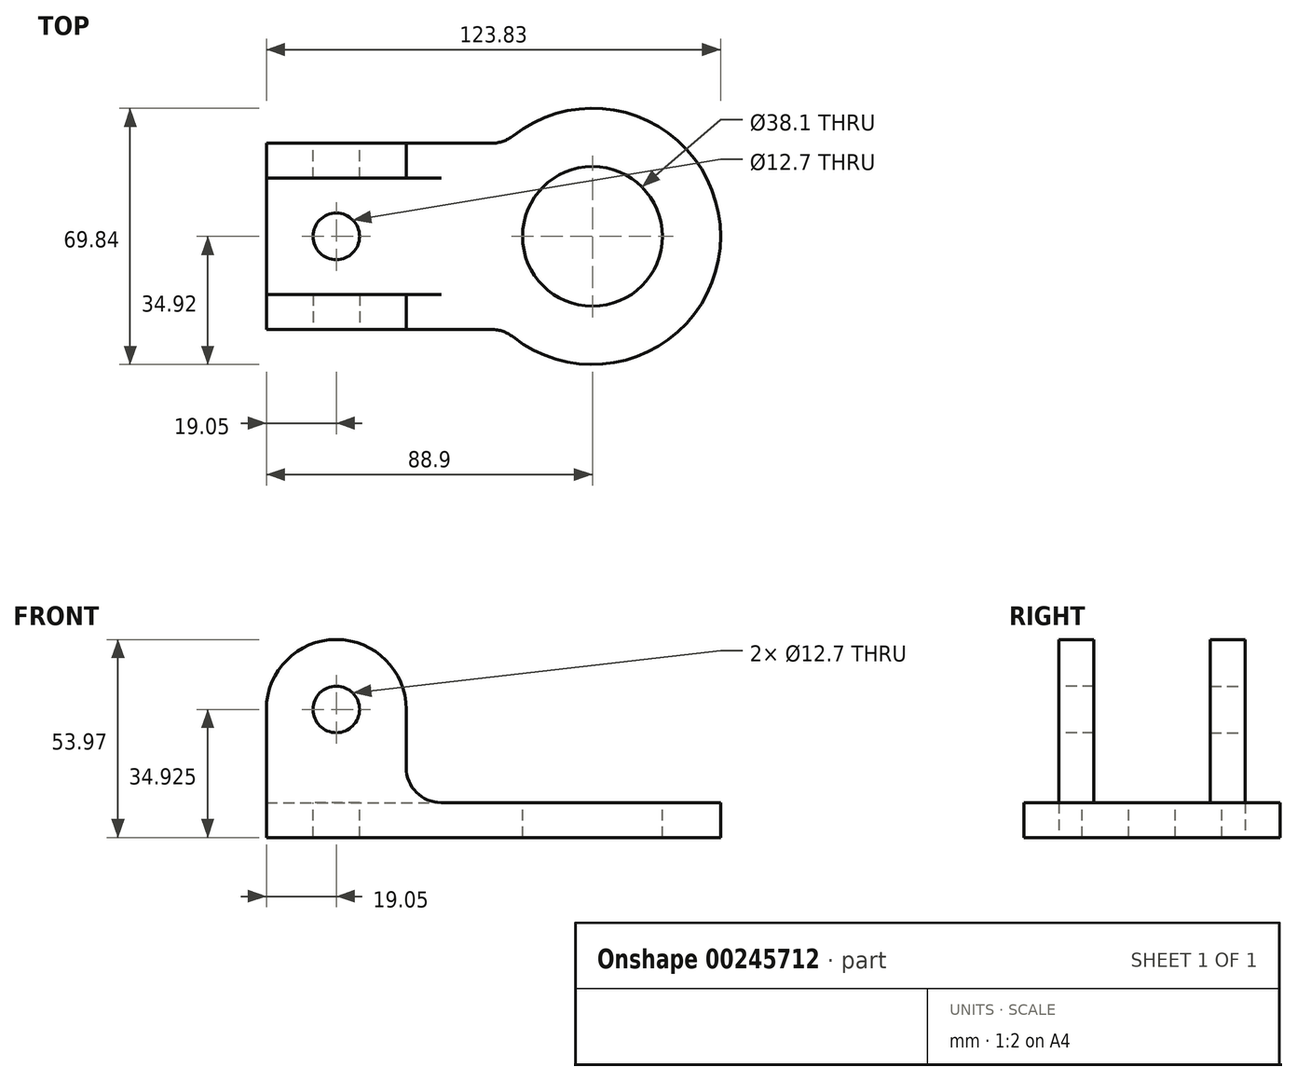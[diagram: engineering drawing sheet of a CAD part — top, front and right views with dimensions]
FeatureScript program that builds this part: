
annotation { "Feature Type Name" : "Feature", "Feature Type Description" : "" }
export const myFeature = defineFeature(function(context is Context, id is Id, definition is map)
    precondition{}
    {
        {
            var Q0;
            Q0=qCreatedBy(makeId("Top.planeOp"),FACE);
            var sketch = newSketch(context, id + "F0", { "sketchPlane" : qUnion([Q0])});
            skLineSegment(sketch, "E0.bottom", {"start": v(0, 0) * mm, "end": v(61.4, 0) * mm});
            skLineSegment(sketch, "E0.top", {"start": v(0, 50.8) * mm, "end": v(61.4, 50.8) * mm});
            skLineSegment(sketch, "E0.left", {"start": v(0, 0) * mm, "end": v(0, 50.8) * mm});
            skArc(sketch, "E1", {"start": v(67.3, -2.04) * mm, "mid": v(123.83, 25.4) * mm, "end": v(67.3, 52.84) * mm});
            skPoint(sketch, "E2.orphan", {"position": v(88.9, 50.8) * mm});
            skPoint(sketch, "E3.orphan", {"position": v(88.9, 0) * mm});
            skPoint(sketch, "E4.visualSharp", {"position": v(64.93, 0) * mm});
            skArc(sketch, "E4.filletArc", {"start": v(67.3, -2.04) * mm, "mid": v(64.52, -0.52) * mm, "end": v(61.4, 0) * mm});
            skPoint(sketch, "E5.visualSharp", {"position": v(64.93, 50.8) * mm});
            skArc(sketch, "E5.filletArc", {"start": v(61.4, 50.8) * mm, "mid": v(64.52, 51.32) * mm, "end": v(67.3, 52.84) * mm});
            skSolve(sketch);
        }
        {
            var Q0;
            Q0 = qSketchRegion(id + "F0", true);
            extrude(context, id + "F1", {"entities" : qUnion([Q0]), "depth" : 9.52 * mm});
        }
        {
            var Q0;
            Q0=makeQuery(id+"F1.opExtrude","CAP_FACE",FACE,{"disambiguationData":[OSD([sQuery(id+"F0.wireOp",EDGE,"E0.bottom"),sQuery(id+"F0.wireOp",EDGE,"E0.top"),sQuery(id+"F0.wireOp",EDGE,"E0.left"),sQuery(id+"F0.wireOp",EDGE,"E1")])],"isStart":false});
            var sketch = newSketch(context, id + "F2", { "sketchPlane" : qUnion([Q0])});
            skCircle(sketch, "E6", {"center": v(88.9, 25.4) * mm, "radius": 19.05 * mm});
            skSolve(sketch);
        }
        {
            var Q0;
            Q0 = qSketchRegion(id + "F2", true);
            extrude(context, id + "F3", {"entities" : qUnion([Q0]), "operationType" : NewBodyOperationType.REMOVE, "oppositeDirection" : true, "depth" : 9.52 * mm});
        }
        {
            var Q0;
            Q0=makeQuery(id+"F1.opExtrude","CAP_FACE",FACE,{"disambiguationData":[OSD([sQuery(id+"F0.wireOp",EDGE,"E0.bottom"),sQuery(id+"F0.wireOp",EDGE,"E0.top"),sQuery(id+"F0.wireOp",EDGE,"E0.left"),sQuery(id+"F0.wireOp",EDGE,"E1"),sQuery(id+"F0.wireOp",EDGE,"E4.filletArc"),sQuery(id+"F0.wireOp",EDGE,"E5.filletArc")])],"isStart":false});
            var sketch = newSketch(context, id + "F4", { "sketchPlane" : qUnion([Q0])});
            skLineSegment(sketch, "E7.bottom", {"start": v(0, 0) * mm, "end": v(38.1, 0) * mm});
            skLineSegment(sketch, "E7.top", {"start": v(0, 9.53) * mm, "end": v(38.1, 9.53) * mm});
            skLineSegment(sketch, "E7.left", {"start": v(0, 0) * mm, "end": v(0, 9.53) * mm});
            skLineSegment(sketch, "E7.right", {"start": v(38.1, 0) * mm, "end": v(38.1, 9.53) * mm});
            skLineSegment(sketch, "E8.bottom", {"start": v(0, 50.8) * mm, "end": v(38.1, 50.8) * mm});
            skLineSegment(sketch, "E8.top", {"start": v(0, 41.28) * mm, "end": v(38.1, 41.28) * mm});
            skLineSegment(sketch, "E8.left", {"start": v(0, 50.8) * mm, "end": v(0, 41.28) * mm});
            skLineSegment(sketch, "E8.right", {"start": v(38.1, 50.8) * mm, "end": v(38.1, 41.28) * mm});
            skSolve(sketch);
        }
        {
            var Q0;
            Q0 = qSketchRegion(id + "F4", true);
            extrude(context, id + "F5", {"entities" : qUnion([Q0]), "operationType" : NewBodyOperationType.ADD, "depth" : 25.4 * mm});
        }
        {
            var Q0;
            Q0=makeQuery(id+"F5.boolean.opBoolean","MERGE",FACE,{"derivedFrom":[makeQuery(id+"F1.opExtrude","SWEPT_FACE",FACE,{"disambiguationData":[OSD([sQuery(id+"F0.wireOp",EDGE,"E0.top")])]}),makeQuery(id+"F5.opExtrude","SWEPT_FACE",FACE,{"disambiguationData":[OSD([sQuery(id+"F4.wireOp",EDGE,"E8.bottom")])]})]});
            var sketch = newSketch(context, id + "F6", { "sketchPlane" : qUnion([Q0])});
            skCircle(sketch, "E9", {"center": v(-19.05, 34.93) * mm, "radius": 19.05 * mm});
            skLineSegment(sketch, "E10", {"start": v(-38.1, 34.93) * mm, "end": v(-38.1, 19.05) * mm});
            skLineSegment(sketch, "E11", {"start": v(-47.62, 9.53) * mm, "end": v(-61.4, 9.53) * mm});
            skPoint(sketch, "E12.visualSharp", {"position": v(-38.1, 9.53) * mm});
            skArc(sketch, "E12.filletArc", {"start": v(-47.62, 9.53) * mm, "mid": v(-40.89, 12.31) * mm, "end": v(-38.1, 19.05) * mm});
            skSolve(sketch);
        }
        {
            var Q0;
            Q0 = qSketchRegion(id + "F6", true);
            extrude(context, id + "F7", {"entities" : qUnion([Q0]), "operationType" : NewBodyOperationType.ADD, "oppositeDirection" : true, "depth" : 9.52 * mm});
        }
        {
            var Q0;
            Q0=makeQuery(id+"F7.boolean.opBoolean","MERGE",FACE,{"derivedFrom":[makeQuery(id+"F5.boolean.opBoolean","MERGE",FACE,{"derivedFrom":[makeQuery(id+"F1.opExtrude","SWEPT_FACE",FACE,{"disambiguationData":[OSD([sQuery(id+"F0.wireOp",EDGE,"E0.top")])]}),makeQuery(id+"F5.opExtrude","SWEPT_FACE",FACE,{"disambiguationData":[OSD([sQuery(id+"F4.wireOp",EDGE,"E8.bottom")])]})]}),makeQuery(id+"F7.opExtrude","CAP_FACE",FACE,{"disambiguationData":[OSD([sQuery(id+"F6.wireOp",EDGE,"E9")])],"isStart":true})]});
            var sketch = newSketch(context, id + "F8", { "sketchPlane" : qUnion([Q0])});
            skCircle(sketch, "E13", {"center": v(-19.05, 34.93) * mm, "radius": 6.35 * mm});
            skSolve(sketch);
        }
        {
            var Q0;
            Q0=makeQuery(id+"F8.imprint","IMPRINT",FACE,{"disambiguationData":[TD([[makeQuery(id+"F8.imprint","IMPRINT",EDGE,{"derivedFrom":sQuery(id+"F8.wireOp",EDGE,"E13")}),1.0]])]});
            extrude(context, id + "F9", {"entities" : qUnion([Q0]), "operationType" : NewBodyOperationType.REMOVE, "oppositeDirection" : true, "depth" : 9.52 * mm});
        }
        {
            var Q0;
            Q0=makeQuery(id+"F5.boolean.opBoolean","MERGE",FACE,{"derivedFrom":[makeQuery(id+"F1.opExtrude","SWEPT_FACE",FACE,{"disambiguationData":[OSD([sQuery(id+"F0.wireOp",EDGE,"E0.bottom")])]}),makeQuery(id+"F5.opExtrude","SWEPT_FACE",FACE,{"disambiguationData":[OSD([sQuery(id+"F4.wireOp",EDGE,"E7.bottom")])]})]});
            var sketch = newSketch(context, id + "F10", { "sketchPlane" : qUnion([Q0])});
            skCircle(sketch, "E14", {"center": v(19.05, 34.93) * mm, "radius": 19.05 * mm});
            skLineSegment(sketch, "E15", {"start": v(38.1, 34.93) * mm, "end": v(38.1, 19.05) * mm});
            skLineSegment(sketch, "E16", {"start": v(47.62, 9.53) * mm, "end": v(61.4, 9.53) * mm});
            skPoint(sketch, "E17.visualSharp", {"position": v(38.1, 9.53) * mm});
            skArc(sketch, "E17.filletArc", {"start": v(38.1, 19.05) * mm, "mid": v(40.89, 12.31) * mm, "end": v(47.62, 9.53) * mm});
            skSolve(sketch);
        }
        {
            var Q0;
            Q0 = qSketchRegion(id + "F10", true);
            extrude(context, id + "F11", {"entities" : qUnion([Q0]), "operationType" : NewBodyOperationType.ADD, "oppositeDirection" : true, "depth" : 9.52 * mm});
        }
        {
            var Q0;
            Q0=makeQuery(id+"F11.boolean.opBoolean","MERGE",FACE,{"derivedFrom":[makeQuery(id+"F5.boolean.opBoolean","MERGE",FACE,{"derivedFrom":[makeQuery(id+"F1.opExtrude","SWEPT_FACE",FACE,{"disambiguationData":[OSD([sQuery(id+"F0.wireOp",EDGE,"E0.bottom")])]}),makeQuery(id+"F5.opExtrude","SWEPT_FACE",FACE,{"disambiguationData":[OSD([sQuery(id+"F4.wireOp",EDGE,"E7.bottom")])]})]}),makeQuery(id+"F11.opExtrude","CAP_FACE",FACE,{"disambiguationData":[OSD([sQuery(id+"F10.wireOp",EDGE,"E14")])],"isStart":true})]});
            var sketch = newSketch(context, id + "F12", { "sketchPlane" : qUnion([Q0])});
            skCircle(sketch, "E18", {"center": v(19.05, 34.93) * mm, "radius": 6.35 * mm});
            skSolve(sketch);
        }
        {
            var Q0;
            Q0 = qSketchRegion(id + "F12", true);
            extrude(context, id + "F13", {"entities" : qUnion([Q0]), "operationType" : NewBodyOperationType.REMOVE, "oppositeDirection" : true, "depth" : 9.52 * mm});
        }
        {
            var Q0;
            Q0=makeQuery(id+"F1.opExtrude","CAP_FACE",FACE,{"disambiguationData":[OSD([sQuery(id+"F0.wireOp",EDGE,"E0.bottom"),sQuery(id+"F0.wireOp",EDGE,"E0.top"),sQuery(id+"F0.wireOp",EDGE,"E0.left"),sQuery(id+"F0.wireOp",EDGE,"E1"),sQuery(id+"F0.wireOp",EDGE,"E4.filletArc"),sQuery(id+"F0.wireOp",EDGE,"E5.filletArc")])],"isStart":false});
            var sketch = newSketch(context, id + "F14", { "sketchPlane" : qUnion([Q0])});
            skCircle(sketch, "E19", {"center": v(19.05, 25.4) * mm, "radius": 6.35 * mm});
            skSolve(sketch);
        }
        {
            var Q0;
            Q0 = qSketchRegion(id + "F14", true);
            extrude(context, id + "F15", {"entities" : qUnion([Q0]), "operationType" : NewBodyOperationType.REMOVE, "oppositeDirection" : true, "depth" : 25.4 * mm});
        }
        {
            var Q0;
            {var subQ0=sQuery(id+"F6.wireOp",EDGE,"E12.filletArc");Q0=makeQuery(id+"F6.imprint","IMPRINT",FACE,{"disambiguationData":[TD([[makeQuery(id+"F6.imprint","IMPRINT",EDGE,{"derivedFrom":subQ0}),-1.0]])]});}
            extrude(context, id + "F16", {"entities" : qUnion([Q0]), "operationType" : NewBodyOperationType.ADD, "oppositeDirection" : true, "depth" : 9.52 * mm});
        }
        {
            var Q0;
            {var subQ0=sQuery(id+"F10.wireOp",EDGE,"E17.filletArc");Q0=makeQuery(id+"F10.imprint","IMPRINT",FACE,{"disambiguationData":[TD([[makeQuery(id+"F10.imprint","IMPRINT",EDGE,{"derivedFrom":subQ0}),-1.0]])]});}
            extrude(context, id + "F17", {"entities" : qUnion([Q0]), "operationType" : NewBodyOperationType.ADD, "oppositeDirection" : true, "depth" : 9.52 * mm});
        }
    });
